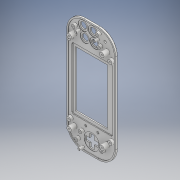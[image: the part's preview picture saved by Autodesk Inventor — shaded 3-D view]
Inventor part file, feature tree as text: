
AUTODESK INVENTOR PART (.ipt)
format: ipt  version: 2019 (Build 230136000, 136)  size: 930,304 bytes
history: native  units: mm
features: sketch x20, extrude x18, fillet x7, chamfer x5, other x2, shell x1
ambient origin geometry x8: Origin, YZ Plane, XZ Plane, XY Plane, X Axis, Y Axis, Z Axis, Center Point
bodies: Solide1 (feature_tree)
feature tree (53):
  extrude  "Extrusion1"  Depth=200.0mm
  chamfer  "Chanfrein1"  Distance=85.0mm
  chamfer  "Chanfrein2"  Distance=42.5mm
  fillet  "Congé3"  Radius=100.0mm
  fillet  "Congé4"  Radius=42.0mm
  shell  "Coque1"  Thickness=20.0mm
  extrude  "Extrusion2"  Depth=20.0mm TaperAngle=60.0deg
  extrude  "Extrusion15"  Depth=30.0mm
  extrude  "Extrusion4"  Depth=15.0mm
  extrude  "Extrusion5"  Depth=2.5mm
  extrude  "Extrusion6"  Depth=2.5mm TaperAngle=0.0deg
  extrude  "Extrusion7"  Depth=108.0mm
  fillet  "Congé6"  Radius=71.0mm
  extrude  "Extrusion10"  Depth=36.5mm
  extrude  "Extrusion13"  Depth=54.0mm
  extrude  "Extrusion14"  Depth=1.0mm
  chamfer  "Chanfrein4"  Distance=220.0mm
  fillet  "Congé14"  Radius=200.0mm
  fillet  "Congé15"  Radius=10.0mm
  fillet  "Congé16"  Radius=50.0mm
  fillet  "Congé17"  Radius=10.0mm
  extrude  "Extrusion8"  Depth=2.5mm
  extrude  "Extrusion12"  Depth=0.25mm
  extrude  "Extrusion11"  Depth=1.0mm TaperAngle=0.0deg
  extrude  "Extrusion16"  Depth=7.5mm
  chamfer  "Chanfrein5"  Distance=7.5mm
  extrude  "Extrusion17"  Depth=7.5mm
  extrude  "Extrusion18"  Depth=7.5mm
  extrude  "Extrusion19"  Depth=122.0mm
  chamfer  "Chanfrein6"  Distance=72.0mm
  extrude  "Extrusion20"  Depth=122.0mm
  other  "Gravure1"
  other  "Gravure2"
  sketch  "Esquisse1"
  sketch  "Esquisse3"
  sketch  "Esquisse4"
  sketch  "Esquisse5"
  sketch  "Esquisse6"
  sketch  "Esquisse7"
  sketch  "Esquisse8"
  sketch  "Esquisse9"
  sketch  "Esquisse11"
  sketch  "Esquisse12"
  sketch  "Esquisse14"
  sketch  "Esquisse15"
  sketch  "Esquisse16"
  sketch  "Esquisse17"
  sketch  "Esquisse18"
  sketch  "Esquisse19"
  sketch  "Esquisse20"
  sketch  "Esquisse21"
  sketch  "Esquisse23"
  sketch  "Esquisse24"
